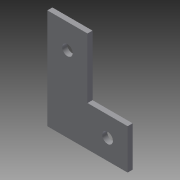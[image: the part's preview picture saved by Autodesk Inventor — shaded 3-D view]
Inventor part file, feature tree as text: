
AUTODESK INVENTOR PART (.ipt)
format: ipt  version: 2013 (Build 170138000, 138)  size: 86,016 bytes
history: native  units: in
note: dims shown in document units (in); Inventor stores cm internally (conversion verified against a paired STEP export)
features: reference x6, sketch x3, extrude x2
ambient origin geometry x8: Origin, YZ Plane, XZ Plane, XY Plane, X Axis, Y Axis, Z Axis, Center Point
bodies: Solid1 (feature_tree)
feature tree (11):
  extrude  "Extrusion1"  Depth=1.0in
  sketch  "Sketch2"  dims[d3=1.0in d4=1.5in]
  sketch  "Sketch3"  dims[d5=0.125in d6=0.0in d7=1.0in d8=0.0in]
  extrude  "Extrusion2"  Depth=1.5in
  sketch  "Sketch1"  dims[d0=2.0in d2=1.0in]
  reference  "Reference1"
  reference  "Reference2"
  reference  "Reference3"
  reference  "Reference4"
  reference  "Reference5"
  reference  "Reference6"
